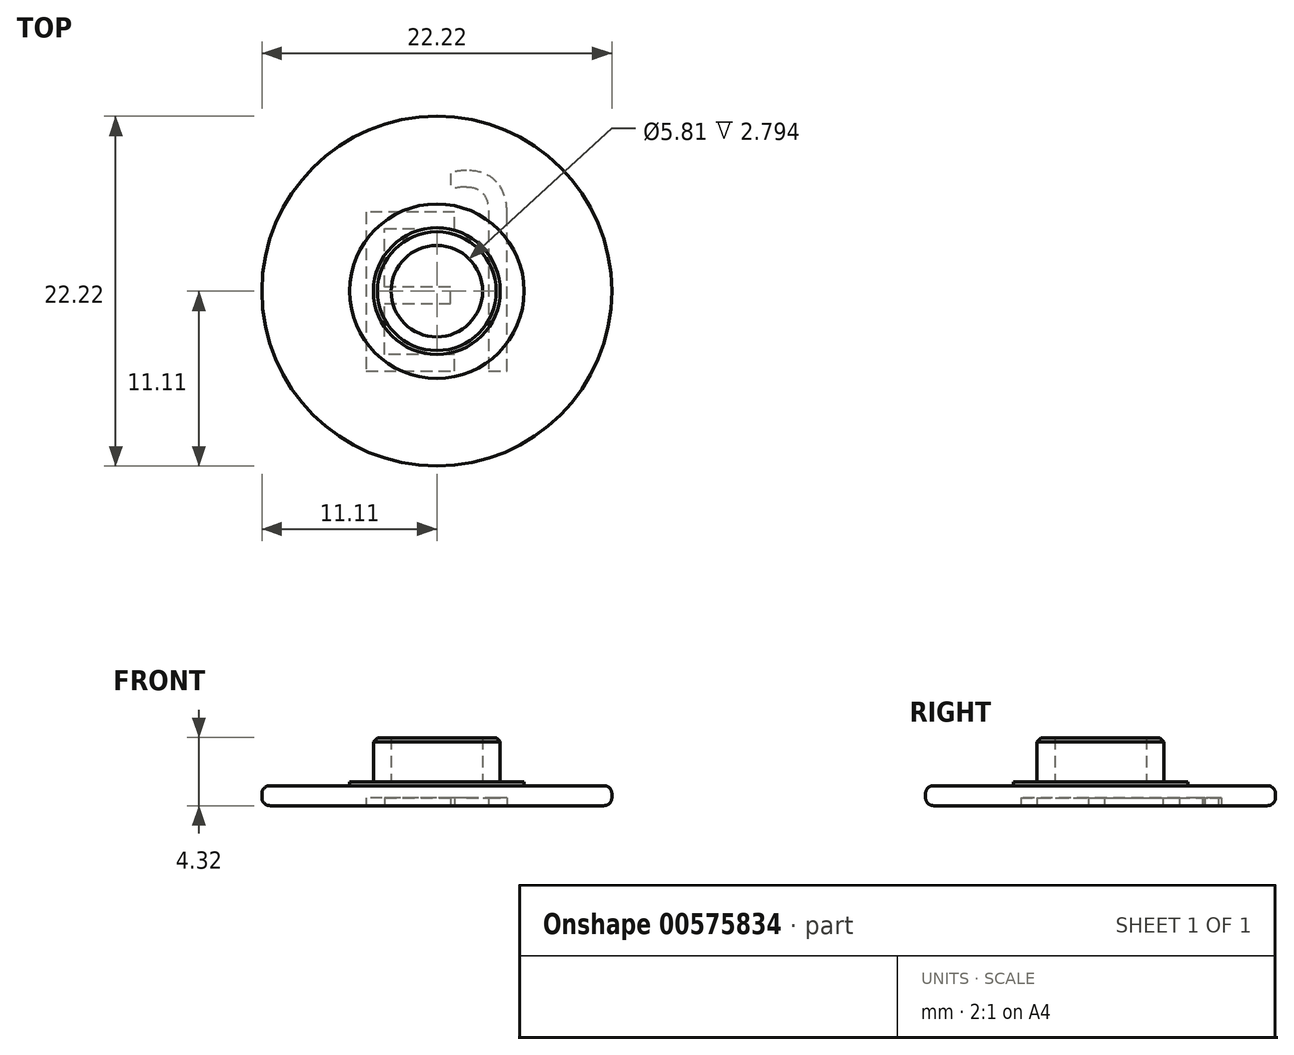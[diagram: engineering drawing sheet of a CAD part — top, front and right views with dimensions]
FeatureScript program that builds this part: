
annotation { "Feature Type Name" : "Feature", "Feature Type Description" : "" }
export const myFeature = defineFeature(function(context is Context, id is Id, definition is map)
    precondition{}
    {
        {
            var Q0;
            Q0=qCreatedBy(makeId("Top.planeOp"),FACE);
            var sketch = newSketch(context, id + "F0", { "sketchPlane" : qUnion([Q0])});
            skCircle(sketch, "E0", {"center": v(0, 0) * mm, "radius": 11.11 * mm});
            skSolve(sketch);
        }
        {
            var Q0;
            Q0 = qSketchRegion(id + "F0", true);
            extrude(context, id + "F1", {"entities" : qUnion([Q0]), "depth" : 1.27 * mm, "offsetDistance" : 25.4 * mm});
        }
        {
            var Q0;
            Q0=makeQuery(id+"F1.opExtrude","CAP_FACE",FACE,{"disambiguationData":[OSD([sQuery(id+"F0.wireOp",EDGE,"E0")])],"isStart":false});
            var sketch = newSketch(context, id + "F2", { "sketchPlane" : qUnion([Q0])});
            skCircle(sketch, "E1", {"center": v(0, 0) * mm, "radius": 4.03 * mm});
            skCircle(sketch, "E2", {"center": v(0, 0) * mm, "radius": 2.9 * mm});
            skSolve(sketch);
        }
        {
            var Q0;
            Q0 = qSketchRegion(id + "F2", true);
            extrude(context, id + "F3", {"entities" : qUnion([Q0]), "operationType" : NewBodyOperationType.ADD, "depth" : 3.05 * mm, "offsetDistance" : 25.4 * mm});
        }
        {
            var Q0;
            {var subQ0=sQuery(id+"F0.wireOp",EDGE,"E0");Q0=makeQuery(id+"F3.boolean.opBoolean","SPLIT",FACE,{"disambiguationData":[TD([makeQuery(id+"F1.opExtrude","SWEPT_FACE",FACE,{"disambiguationData":[OSD([subQ0])]})])],"derivedFrom":makeQuery(id+"F1.opExtrude","CAP_FACE",FACE,{"disambiguationData":[OSD([subQ0])],"isStart":false})});}
            var sketch = newSketch(context, id + "F4", { "sketchPlane" : qUnion([Q0])});
            skCircle(sketch, "E3", {"center": v(0, 0) * mm, "radius": 5.54 * mm});
            skSolve(sketch);
        }
        {
            var Q0;
            Q0 = qSketchRegion(id + "F4", true);
            extrude(context, id + "F5", {"entities" : qUnion([Q0]), "operationType" : NewBodyOperationType.ADD, "depth" : 0.25 * mm, "offsetDistance" : 25.4 * mm});
        }
        {
            var Q0;
            Q0=makeQuery(id+"F1.opExtrude","SWEPT_FACE",FACE,{"disambiguationData":[OSD([sQuery(id+"F0.wireOp",EDGE,"E0")])]});
            fillet(context, id + "F6", {"entities" : qUnion([Q0]), "radius" : 0.5 * mm, "tangentPropagation" : true, "allowEdgeOverflow" : false});
        }
        {
            var Q0;
            Q0=makeQuery(id+"F3.opExtrude","CAP_EDGE",EDGE,{"disambiguationData":[OSD([sQuery(id+"F2.wireOp",EDGE,"E1")])],"isStart":false});
            chamfer(context, id + "F7", {"entities" : qUnion([Q0]), "width" : 0.25 * mm, "tangentPropagation" : true});
        }
        {
            var Q0;
            Q0=makeQuery(id+"F1.opExtrude","CAP_FACE",FACE,{"disambiguationData":[OSD([sQuery(id+"F0.wireOp",EDGE,"E0")])],"isStart":true});
            var sketch = newSketch(context, id + "F8", { "sketchPlane" : qUnion([Q0])});
            skText(sketch, "E4", { "text": "EJ", "fontName": "OpenSans-Regular.ttf"});
            const initialGuessF8  = {"E4": [-0.00587, -0.00501, 1, 0, 0.01016]};
            skSetInitialGuess(sketch, initialGuessF8);
            skSolve(sketch);
        }
        {
            var Q0;
            Q0 = qSketchRegion(id + "F8", true);
            extrude(context, id + "F9", {"entities" : qUnion([Q0]), "operationType" : NewBodyOperationType.REMOVE, "oppositeDirection" : true, "depth" : 0.5 * mm, "offsetDistance" : 25.4 * mm});
        }
    });
